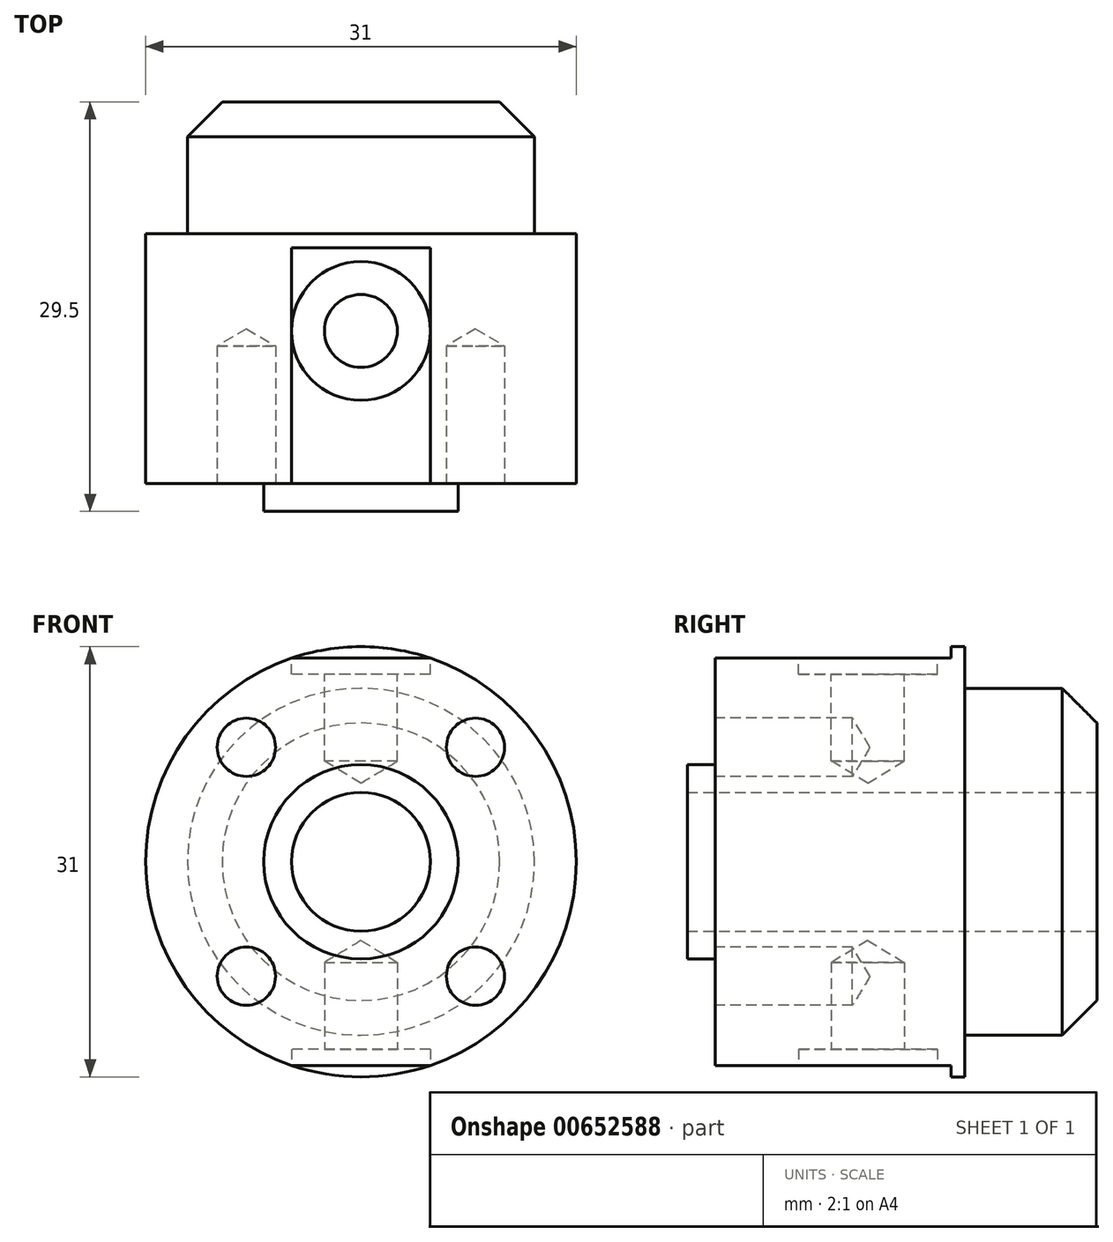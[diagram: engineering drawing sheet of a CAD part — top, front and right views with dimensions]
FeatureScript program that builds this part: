
annotation { "Feature Type Name" : "Feature", "Feature Type Description" : "" }
export const myFeature = defineFeature(function(context is Context, id is Id, definition is map)
    precondition{}
    {
        {
            var Q0;
            Q0=qCreatedBy(makeId("Right.planeOp"),FACE);
            var sketch = newSketch(context, id + "F0", { "sketchPlane" : qUnion([Q0])});
            skLineSegment(sketch, "E0", {"start": v(0, 5) * mm, "end": v(0, 15.5) * mm});
            skLineSegment(sketch, "E1", {"start": v(0, 15.5) * mm, "end": v(-18, 15.5) * mm});
            skLineSegment(sketch, "E2", {"start": v(-18, 15.5) * mm, "end": v(-18, 7) * mm});
            skLineSegment(sketch, "E3", {"start": v(-18, 7) * mm, "end": v(-20, 7) * mm});
            skLineSegment(sketch, "E4", {"start": v(-20, 7) * mm, "end": v(-20, 5) * mm});
            skPoint(sketch, "E5.startSnap0", {"position": v(0, 7.75) * mm});
            skLineSegment(sketch, "E6", {"start": v(0, 5) * mm, "end": v(-20, 5) * mm});
            skPoint(sketch, "E7.end.orphan", {"position": v(0, 0) * mm});
            skPoint(sketch, "E8.orphan", {"position": v(-20, 0) * mm});
            skLineSegment(sketch, "E9", {"start": v(0, 0) * mm, "end": v(-26.18, 0) * mm, "construction": true});
            skSolve(sketch);
        }
        {
            var Q0;
            Q0 = qSketchRegion(id + "F0", true);
            var Q1;
            Q1=sQuery(id+"F0.wireOp",EDGE,"E9");
            revolve(context, id + "F1", {"entities" : qUnion([Q0]), "axis" : qUnion([Q1]), "revolveType" : RevolveType.FULL});
        }
        {
            var Q0;
            Q0=makeQuery(id+"F1.opRevolve","SWEPT_FACE",FACE,{"disambiguationData":[OSD([sQuery(id+"F0.wireOp",EDGE,"E2")])]});
            var sketch = newSketch(context, id + "F2", { "sketchPlane" : qUnion([Q0])});
            skCircle(sketch, "E10", {"center": v(8.25, 8.25) * mm, "radius": 1.5 * mm});
            skCircle(sketch, "E11.1.0", {"center": v(-8.25, 8.25) * mm, "radius": 1.5 * mm});
            skCircle(sketch, "E11.2.0", {"center": v(-8.25, -8.25) * mm, "radius": 1.5 * mm});
            skCircle(sketch, "E11.3.0", {"center": v(8.25, -8.25) * mm, "radius": 1.5 * mm});
            skPoint(sketch, "E11.center", {"position": v(0, 0) * mm});
            skSolve(sketch);
        }
        {
            var Q0;
            Q0 = qSketchRegion(id + "F2", true);
            extrude(context, id + "F3", {"entities" : qUnion([Q0]), "operationType" : NewBodyOperationType.REMOVE, "oppositeDirection" : true, "depth" : 7.5 * mm, "offsetDistance" : 25 * mm});
        }
        {
            var Q0;
            Q0=makeQuery(id+"F1.opRevolve","SWEPT_FACE",FACE,{"disambiguationData":[OSD([sQuery(id+"F0.wireOp",EDGE,"E2")])]});
            var sketch = newSketch(context, id + "F4", { "sketchPlane" : qUnion([Q0])});
            skCircle(sketch, "E12", {"center": v(8.25, 8.25) * mm, "radius": 1.53 * mm});
            skCircle(sketch, "E13.1.0", {"center": v(-8.25, 8.25) * mm, "radius": 1.53 * mm});
            skCircle(sketch, "E13.2.0", {"center": v(-8.25, -8.25) * mm, "radius": 1.53 * mm});
            skCircle(sketch, "E13.3.0", {"center": v(8.25, -8.25) * mm, "radius": 1.53 * mm});
            skPoint(sketch, "E13.center", {"position": v(0, 0) * mm});
            skSolve(sketch);
        }
        {
            var Q0;
            Q0=sQuery(id+"F4.wireOp",VERTEX,"E12.center");
            var Q1;
            Q1=sQuery(id+"F4.wireOp",VERTEX,"E13.1.0.center");
            var Q2;
            Q2=sQuery(id+"F4.wireOp",VERTEX,"E13.2.0.center");
            var Q3;
            Q3=sQuery(id+"F4.wireOp",VERTEX,"E13.3.0.center");
            var Q4;
            Q4=makeQuery(id+"F1.opRevolve","SWEPT_BODY",BODY,{"disambiguationData":[OSD([sQuery(id+"F0.wireOp",EDGE,"E0"),sQuery(id+"F0.wireOp",EDGE,"E1"),sQuery(id+"F0.wireOp",EDGE,"E2"),sQuery(id+"F0.wireOp",EDGE,"E3"),sQuery(id+"F0.wireOp",EDGE,"E4"),sQuery(id+"F0.wireOp",EDGE,"E6")])]});
            hole(context, id + "F5", {"style" : HoleStyle.SIMPLE, "endStyle" : HoleEndStyle.BLIND, "standardTappedOrClearance" : lookupTablePath({ "standard" : "ISO", "engagement" : "75%", "pitch" : "0.8 mm", "size" : "M5", "type" : "Tapped" }), "standardBlindInLast" : lookupTablePath({ "standard" : "ISO", "engagement" : "75%", "pitch" : "0.8 mm", "size" : "M5", "type" : "Tapped" }), "holeDiameter" : 4.2 * mm, "majorDiameter" : 5 * mm, "showTappedDepth" : true, "holeDepth" : 9.9 * mm, "isTappedThrough" : true, "tappedDepth" : 7.5 * mm, "tapClearance" : 3, "locations" : qUnion([Q0, Q1, Q2, Q3]), "scope" : qUnion([Q4])});
        }
        {
            var Q0;
            Q0=qCreatedBy(makeId("Top.planeOp"),FACE);
            cPlane(context, id + "F6", {"entities" : qUnion([Q0]), "cplaneType" : CPlaneType.OFFSET, "offset" : 15.5 * mm, "width" : 150 * mm, "height" : 150 * mm});
        }
        {
            var Q0;
            Q0=qCreatedBy(id+"F6.planeOp",FACE);
            var sketch = newSketch(context, id + "F7", { "sketchPlane" : qUnion([Q0])});
            skCircle(sketch, "E14", {"center": v(0, -7) * mm, "radius": 5 * mm});
            skSolve(sketch);
        }
        {
            var Q0;
            Q0 = qSketchRegion(id + "F7", true);
            extrude(context, id + "F8", {"entities" : qUnion([Q0]), "operationType" : NewBodyOperationType.REMOVE, "oppositeDirection" : true, "depth" : 2 * mm, "offsetDistance" : 25 * mm});
        }
        {
            var Q0;
            Q0=qCreatedBy(id+"F6.planeOp",FACE);
            var sketch = newSketch(context, id + "F9", { "sketchPlane" : qUnion([Q0])});
            skCircle(sketch, "E15", {"center": v(0, -7) * mm, "radius": 2.69 * mm});
            skSolve(sketch);
        }
        {
            var Q0;
            Q0=sQuery(id+"F9.wireOp",VERTEX,"E15.center");
            var Q1;
            Q1=makeQuery(id+"F1.opRevolve","SWEPT_BODY",BODY,{"disambiguationData":[OSD([sQuery(id+"F0.wireOp",EDGE,"E0"),sQuery(id+"F0.wireOp",EDGE,"E1"),sQuery(id+"F0.wireOp",EDGE,"E2"),sQuery(id+"F0.wireOp",EDGE,"E3"),sQuery(id+"F0.wireOp",EDGE,"E4"),sQuery(id+"F0.wireOp",EDGE,"E6")])]});
            hole(context, id + "F10", {"style" : HoleStyle.SIMPLE, "endStyle" : HoleEndStyle.BLIND, "standardTappedOrClearance" : lookupTablePath({ "standard" : "ISO", "engagement" : "75%", "pitch" : "0.75 mm", "size" : "M6", "type" : "Tapped" }), "standardBlindInLast" : lookupTablePath({ "standard" : "ISO", "engagement" : "75%", "pitch" : "0.75 mm", "size" : "M6", "type" : "Tapped" }), "holeDiameter" : 5.25 * mm, "majorDiameter" : 6 * mm, "showTappedDepth" : true, "holeDepth" : 6.25 * mm, "isTappedThrough" : true, "tappedDepth" : 6.25 * mm, "tapClearance" : 0, "locations" : qUnion([Q0]), "scope" : qUnion([Q1])});
        }
        {
            var Q0;
            Q0=qCreatedBy(makeId("Top.planeOp"),FACE);
            cPlane(context, id + "F11", {"entities" : qUnion([Q0]), "cplaneType" : CPlaneType.OFFSET, "offset" : 15.5 * mm, "oppositeDirection" : true, "width" : 150 * mm, "height" : 150 * mm});
        }
        {
            var Q0;
            Q0=qCreatedBy(id+"F11.planeOp",FACE);
            var sketch = newSketch(context, id + "F12", { "sketchPlane" : qUnion([Q0])});
            skCircle(sketch, "E16", {"center": v(0, -7) * mm, "radius": 5 * mm});
            skSolve(sketch);
        }
        {
            var Q0;
            Q0 = qSketchRegion(id + "F12", true);
            extrude(context, id + "F13", {"entities" : qUnion([Q0]), "operationType" : NewBodyOperationType.REMOVE, "depth" : 2 * mm, "offsetDistance" : 25 * mm});
        }
        {
            var Q0;
            Q0=makeQuery(id+"F13.boolean.opBoolean","COPY",FACE,{"derivedFrom":makeQuery(id+"F13.opExtrude","CAP_FACE",FACE,{"disambiguationData":[OSD([sQuery(id+"F12.wireOp",EDGE,"E16")])],"isStart":false})});
            var sketch = newSketch(context, id + "F14", { "sketchPlane" : qUnion([Q0])});
            skCircle(sketch, "E17", {"center": v(0, 7) * mm, "radius": 2.26 * mm});
            skSolve(sketch);
        }
        {
            var Q0;
            Q0=sQuery(id+"F14.wireOp",VERTEX,"E17.center");
            var Q1;
            Q1=makeQuery(id+"F1.opRevolve","SWEPT_BODY",BODY,{"disambiguationData":[OSD([sQuery(id+"F0.wireOp",EDGE,"E0"),sQuery(id+"F0.wireOp",EDGE,"E1"),sQuery(id+"F0.wireOp",EDGE,"E2"),sQuery(id+"F0.wireOp",EDGE,"E3"),sQuery(id+"F0.wireOp",EDGE,"E4"),sQuery(id+"F0.wireOp",EDGE,"E6")])]});
            hole(context, id + "F15", {"style" : HoleStyle.SIMPLE, "endStyle" : HoleEndStyle.BLIND, "standardTappedOrClearance" : lookupTablePath({ "standard" : "ISO", "engagement" : "75%", "pitch" : "0.75 mm", "size" : "M6", "type" : "Tapped" }), "standardBlindInLast" : lookupTablePath({ "standard" : "ISO", "engagement" : "75%", "pitch" : "0.75 mm", "size" : "M6", "type" : "Tapped" }), "holeDiameter" : 5.25 * mm, "majorDiameter" : 6 * mm, "showTappedDepth" : true, "holeDepth" : 6.25 * mm, "isTappedThrough" : true, "tappedDepth" : 6.25 * mm, "tapClearance" : 0, "locations" : qUnion([Q0]), "scope" : qUnion([Q1])});
        }
        {
            var Q0;
            Q0=makeQuery(id+"F1.opRevolve","SWEPT_FACE",FACE,{"disambiguationData":[OSD([sQuery(id+"F0.wireOp",EDGE,"E0")])]});
            var sketch = newSketch(context, id + "F16", { "sketchPlane" : qUnion([Q0])});
            skCircle(sketch, "E18", {"center": v(0, 0) * mm, "radius": 12.5 * mm});
            skCircle(sketch, "E19", {"center": v(0, 0) * mm, "radius": 5 * mm});
            skSolve(sketch);
        }
        {
            var Q0;
            Q0 = qSketchRegion(id + "F16", true);
            extrude(context, id + "F17", {"entities" : qUnion([Q0]), "operationType" : NewBodyOperationType.ADD, "depth" : 9.5 * mm, "offsetDistance" : 25 * mm});
        }
        {
            var Q0;
            Q0=makeQuery(id+"F17.opExtrude","CAP_EDGE",EDGE,{"disambiguationData":[OSD([sQuery(id+"F16.wireOp",EDGE,"E18")])],"isStart":false});
            chamfer(context, id + "F18", {"entities" : qUnion([Q0]), "width" : 2.5 * mm, "tangentPropagation" : true});
        }
        {
            var Q0;
            Q0=makeQuery(id+"F1.opRevolve","SWEPT_FACE",FACE,{"disambiguationData":[OSD([sQuery(id+"F0.wireOp",EDGE,"E2")])]});
            var sketch = newSketch(context, id + "F19", { "sketchPlane" : qUnion([Q0])});
            skArc(sketch, "E20", {"start": v(5, 14.67) * mm, "mid": v(0, 15.5) * mm, "end": v(-5, 14.67) * mm});
            skLineSegment(sketch, "E21", {"start": v(5, -14.67) * mm, "end": v(-5, -14.67) * mm});
            skLineSegment(sketch, "E22", {"start": v(5, 14.67) * mm, "end": v(-5, 14.67) * mm});
            skArc(sketch, "E23.trimOffspring", {"start": v(-5, -14.67) * mm, "mid": v(0, -15.5) * mm, "end": v(5, -14.67) * mm});
            skSolve(sketch);
        }
        {
            var Q0;
            Q0 = qSketchRegion(id + "F19", true);
            extrude(context, id + "F20", {"entities" : qUnion([Q0]), "operationType" : NewBodyOperationType.REMOVE, "oppositeDirection" : true, "depth" : 17 * mm, "offsetDistance" : 25 * mm});
        }
    });
